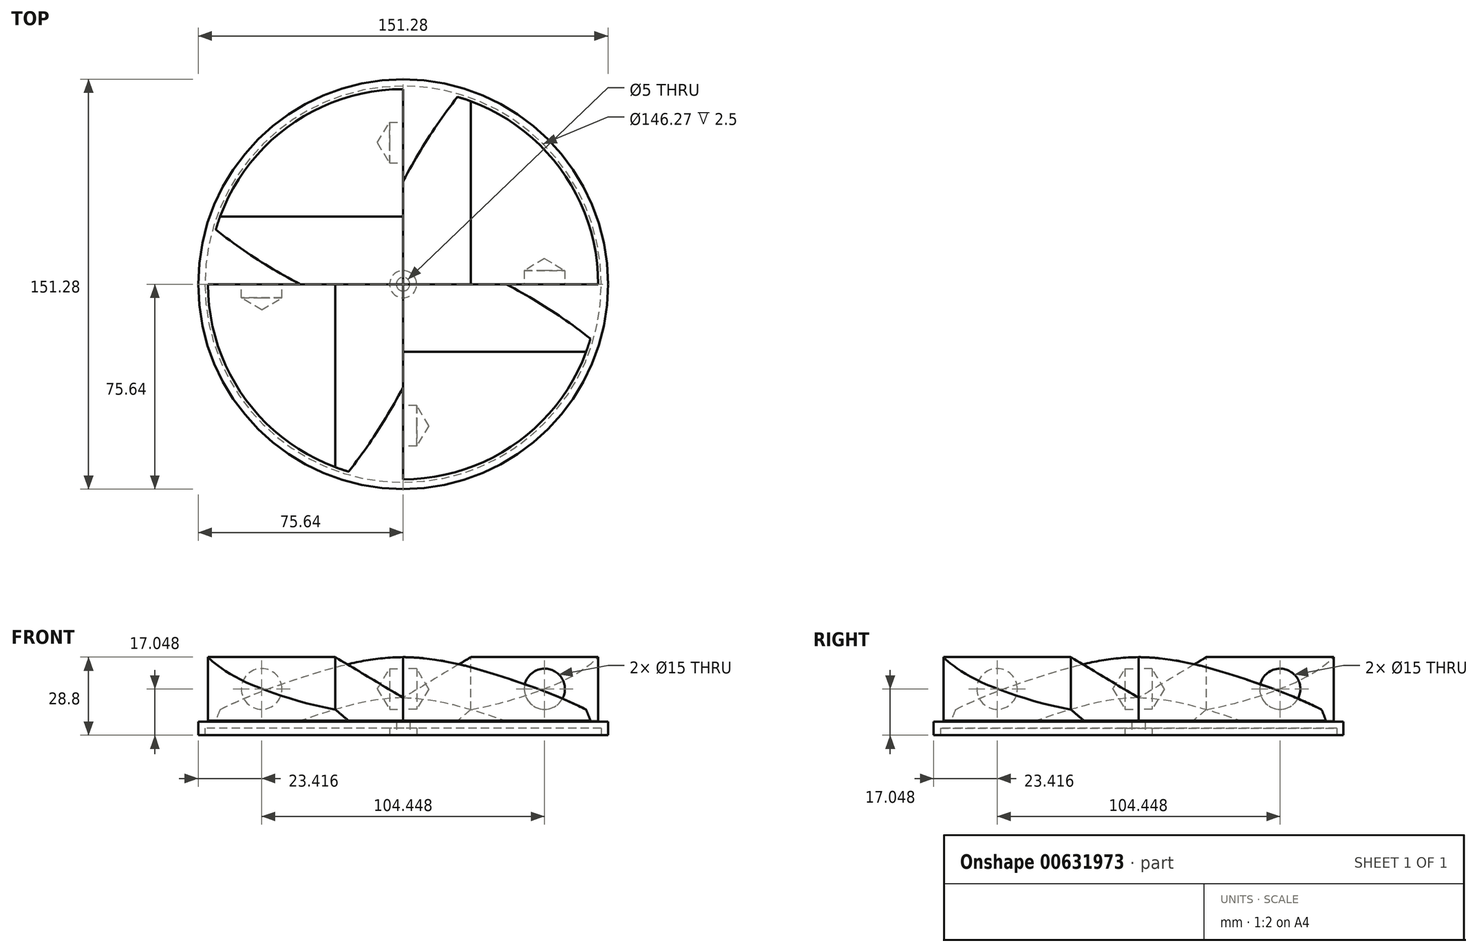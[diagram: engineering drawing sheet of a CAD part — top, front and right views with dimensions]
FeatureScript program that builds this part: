
annotation { "Feature Type Name" : "Feature", "Feature Type Description" : "" }
export const myFeature = defineFeature(function(context is Context, id is Id, definition is map)
    precondition{}
    {
        {
            var Q0;
            Q0=qCreatedBy(makeId("Top.planeOp"),FACE);
            var sketch = newSketch(context, id + "F0", { "sketchPlane" : qUnion([Q0])});
            skCircle(sketch, "E0", {"center": v(0, 0) * mm, "radius": 75.64 * mm});
            skSolve(sketch);
        }
        {
            var Q0;
            Q0=makeQuery(id+"F0.imprint","IMPRINT",FACE,{"disambiguationData":[TD([[makeQuery(id+"F0.imprint","IMPRINT",EDGE,{"derivedFrom":sQuery(id+"F0.wireOp",EDGE,"E0")}),1.0]])]});
            extrude(context, id + "F1", {"entities" : qUnion([Q0]), "depth" : 5 * mm, "offsetDistance" : 25 * mm});
        }
        {
            var Q0;
            Q0=makeQuery(id+"F1.opExtrude","CAP_FACE",FACE,{"disambiguationData":[OSD([sQuery(id+"F0.wireOp",EDGE,"E0")])],"isStart":true});
            var sketch = newSketch(context, id + "F2", { "sketchPlane" : qUnion([Q0])});
            skLineSegment(sketch, "E1", {"start": v(0, 0) * mm, "end": v(-75.64, 0) * mm});
            skSolve(sketch);
        }
        {
            var Q0;
            Q0=sQuery(id+"F2.wireOp",VERTEX,"E1.start");
            var Q1;
            Q1=makeQuery(id+"F1.opExtrude","SWEPT_BODY",BODY,{"disambiguationData":[OSD([sQuery(id+"F0.wireOp",EDGE,"E0")])]});
            hole(context, id + "F3", {"style" : HoleStyle.SIMPLE, "endStyle" : HoleEndStyle.BLIND, "holeDiameter" : 5 * mm, "majorDiameter" : 5 * mm, "holeDepth" : 35 * mm, "isTappedThrough" : true, "tappedDepth" : 12 * mm, "tapClearance" : 3, "locations" : qUnion([Q0]), "scope" : qUnion([Q1])});
        }
        {
            var Q0;
            Q0=qCreatedBy(makeId("Front.planeOp"),FACE);
            var sketch = newSketch(context, id + "F4", { "sketchPlane" : qUnion([Q0])});
            skLineSegment(sketch, "E2", {"start": v(0, 28.8) * mm, "end": v(0, 5.3) * mm});
            skLineSegment(sketch, "E3", {"start": v(0, 5.3) * mm, "end": v(75.31, 5.3) * mm});
            skFitSpline(sketch, "E4", {"points": [v(75.31, 5.3) * mm, v(37.34, 21.33) * mm, v(0, 28.8) * mm], "startDerivative": vector(-82.04, 46.6) * mm, "endDerivative": vector(-85.16, 0.97) * mm});
            skSolve(sketch);
        }
        {
            var Q0;
            Q0=makeQuery(id+"F4.imprint","IMPRINT",FACE,{"disambiguationData":[TD([[makeQuery(id+"F4.imprint","IMPRINT",EDGE,{"derivedFrom":sQuery(id+"F4.wireOp",EDGE,"E2")}),1.0]])]});
            extrude(context, id + "F5", {"entities" : qUnion([Q0]), "depth" : 73 * mm, "offsetDistance" : 25 * mm});
        }
        {
            var Q0;
            Q0=makeQuery(id+"F5.opExtrude","SWEPT_FACE",FACE,{"disambiguationData":[OSD([sQuery(id+"F4.wireOp",EDGE,"E2")])]});
            var sketch = newSketch(context, id + "F6", { "sketchPlane" : qUnion([Q0])});
            skLineSegment(sketch, "E5", {"start": v(20.11, 17.05) * mm, "end": v(52.22, 17.05) * mm});
            skPoint(sketch, "E5.startSnap0", {"position": v(0, 17.05) * mm});
            skSolve(sketch);
        }
        {
            var Q0;
            Q0=sQuery(id+"F6.wireOp",VERTEX,"E5.end");
            var Q1;
            Q1=makeQuery(id+"F5.opExtrude","SWEPT_BODY",BODY,{"disambiguationData":[OSD([sQuery(id+"F4.wireOp",EDGE,"E2"),sQuery(id+"F4.wireOp",EDGE,"E3"),sQuery(id+"F4.wireOp",EDGE,"E4")])]});
            hole(context, id + "F7", {"style" : HoleStyle.SIMPLE, "endStyle" : HoleEndStyle.BLIND, "holeDiameter" : 15 * mm, "majorDiameter" : 5 * mm, "holeDepth" : 5 * mm, "isTappedThrough" : true, "tappedDepth" : 12 * mm, "tapClearance" : 3, "locations" : qUnion([Q0]), "scope" : qUnion([Q1])});
        }
        {
            var Q0;
            Q0=makeQuery(id+"F5.opExtrude","CAP_EDGE",EDGE,{"disambiguationData":[OSD([sQuery(id+"F4.wireOp",EDGE,"E4")])],"isStart":true});
            chamfer(context, id + "F8", {"entities" : qUnion([Q0]), "chamferType" : ChamferType.TWO_OFFSETS, "width1" : 25 * mm, "oppositeDirection" : false, "width2" : 15 * mm, "tangentPropagation" : true});
        }
        {
            var Q0;
            Q0=makeQuery(id+"F5.opExtrude","SWEPT_BODY",BODY,{"disambiguationData":[OSD([sQuery(id+"F4.wireOp",EDGE,"E2"),sQuery(id+"F4.wireOp",EDGE,"E3"),sQuery(id+"F4.wireOp",EDGE,"E4")])]});
            var Q1;
            Q1=makeQuery(id+"F5.opExtrude","CAP_EDGE",EDGE,{"disambiguationData":[OSD([sQuery(id+"F4.wireOp",EDGE,"E2")])],"isStart":true});
            transform(context, id + "F9", {"entities" : qUnion([Q0]), "transformType" : TransformType.ROTATION, "transformAxis" : qUnion([Q1]), "angle" : 90 * degree, "makeCopy" : true});
        }
        {
            var Q0;
            Q0=makeQuery(id+"F9.opPattern","COPY",BODY,{"derivedFrom":makeQuery(id+"F5.opExtrude","SWEPT_BODY",BODY,{"disambiguationData":[OSD([sQuery(id+"F4.wireOp",EDGE,"E2"),sQuery(id+"F4.wireOp",EDGE,"E3"),sQuery(id+"F4.wireOp",EDGE,"E4")])]}),"instanceName":"1"});
            var Q1;
            Q1=makeQuery(id+"F5.opExtrude","CAP_EDGE",EDGE,{"disambiguationData":[OSD([sQuery(id+"F4.wireOp",EDGE,"E2")])],"isStart":true});
            transform(context, id + "F10", {"entities" : qUnion([Q0]), "transformType" : TransformType.ROTATION, "transformAxis" : qUnion([Q1]), "angle" : 90 * degree, "makeCopy" : true});
        }
        {
            var Q0;
            Q0=makeQuery(id+"F10.opPattern","COPY",BODY,{"derivedFrom":makeQuery(id+"F9.opPattern","COPY",BODY,{"derivedFrom":makeQuery(id+"F5.opExtrude","SWEPT_BODY",BODY,{"disambiguationData":[OSD([sQuery(id+"F4.wireOp",EDGE,"E2"),sQuery(id+"F4.wireOp",EDGE,"E3"),sQuery(id+"F4.wireOp",EDGE,"E4")])]}),"instanceName":"1"}),"instanceName":"1"});
            var Q1;
            Q1=makeQuery(id+"F5.opExtrude","CAP_EDGE",EDGE,{"disambiguationData":[OSD([sQuery(id+"F4.wireOp",EDGE,"E2")])],"isStart":true});
            transform(context, id + "F11", {"entities" : qUnion([Q0]), "transformType" : TransformType.ROTATION, "transformAxis" : qUnion([Q1]), "angle" : 90 * degree, "makeCopy" : true});
        }
        {
            var Q0;
            Q0=qCreatedBy(makeId("Top.planeOp"),FACE);
            var sketch = newSketch(context, id + "F12", { "sketchPlane" : qUnion([Q0])});
            skCircle(sketch, "E6", {"center": v(0, 0) * mm, "radius": 72.02 * mm});
            skSolve(sketch);
        }
        {
            var Q0;
            Q0=makeQuery(id+"F12.imprint","IMPRINT",FACE,{"disambiguationData":[TD([[makeQuery(id+"F12.imprint","IMPRINT",EDGE,{"derivedFrom":sQuery(id+"F12.wireOp",EDGE,"E6")}),1.0]])]});
            extrude(context, id + "F13", {"entities" : qUnion([Q0]), "depth" : 44 * mm, "offsetDistance" : 25 * mm});
        }
        {
            var Q0;
            Q0=makeQuery(id+"F13.opExtrude","SWEPT_BODY",BODY,{"disambiguationData":[OSD([sQuery(id+"F12.wireOp",EDGE,"E6")])]});
            var Q1;
            Q1=makeQuery(id+"F10.opPattern","COPY",BODY,{"derivedFrom":makeQuery(id+"F9.opPattern","COPY",BODY,{"derivedFrom":makeQuery(id+"F5.opExtrude","SWEPT_BODY",BODY,{"disambiguationData":[OSD([sQuery(id+"F4.wireOp",EDGE,"E2"),sQuery(id+"F4.wireOp",EDGE,"E3"),sQuery(id+"F4.wireOp",EDGE,"E4")])]}),"instanceName":"1"}),"instanceName":"1"});
            booleanBodies(context, id + "F14", {"operationType" : BooleanOperationType.INTERSECTION, "tools" : qUnion([Q0, Q1])});
        }
        {
            var Q0;
            Q0=makeQuery(id+"F9.opPattern","COPY",BODY,{"derivedFrom":makeQuery(id+"F5.opExtrude","SWEPT_BODY",BODY,{"disambiguationData":[OSD([sQuery(id+"F4.wireOp",EDGE,"E2"),sQuery(id+"F4.wireOp",EDGE,"E3"),sQuery(id+"F4.wireOp",EDGE,"E4")])]}),"instanceName":"1"});
            deleteBodies(context, id + "F15", {"entities" : qUnion([Q0])});
        }
        {
            var Q0;
            Q0=makeQuery(id+"F11.opPattern","COPY",BODY,{"derivedFrom":makeQuery(id+"F10.opPattern","COPY",BODY,{"derivedFrom":makeQuery(id+"F9.opPattern","COPY",BODY,{"derivedFrom":makeQuery(id+"F5.opExtrude","SWEPT_BODY",BODY,{"disambiguationData":[OSD([sQuery(id+"F4.wireOp",EDGE,"E2"),sQuery(id+"F4.wireOp",EDGE,"E3"),sQuery(id+"F4.wireOp",EDGE,"E4")])]}),"instanceName":"1"}),"instanceName":"1"}),"instanceName":"1"});
            deleteBodies(context, id + "F16", {"entities" : qUnion([Q0])});
        }
        {
            var Q0;
            Q0=makeQuery(id+"F5.opExtrude","SWEPT_BODY",BODY,{"disambiguationData":[OSD([sQuery(id+"F4.wireOp",EDGE,"E2"),sQuery(id+"F4.wireOp",EDGE,"E3"),sQuery(id+"F4.wireOp",EDGE,"E4")])]});
            deleteBodies(context, id + "F17", {"entities" : qUnion([Q0])});
        }
        {
            var Q0;
            Q0=makeQuery(id+"F14.opBoolean","INTERSECT",BODY,{"derivedFrom":[makeQuery(id+"F10.opPattern","COPY",BODY,{"derivedFrom":makeQuery(id+"F9.opPattern","COPY",BODY,{"derivedFrom":makeQuery(id+"F5.opExtrude","SWEPT_BODY",BODY,{"disambiguationData":[OSD([sQuery(id+"F4.wireOp",EDGE,"E2"),sQuery(id+"F4.wireOp",EDGE,"E3"),sQuery(id+"F4.wireOp",EDGE,"E4")])]}),"instanceName":"1"}),"instanceName":"1"}),makeQuery(id+"F13.opExtrude","SWEPT_BODY",BODY,{"disambiguationData":[OSD([sQuery(id+"F12.wireOp",EDGE,"E6")])]})]});
            var Q1;
            Q1=makeQuery(id+"F10.opPattern","COPY",EDGE,{"derivedFrom":makeQuery(id+"F9.opPattern","COPY",EDGE,{"derivedFrom":makeQuery(id+"F5.opExtrude","CAP_EDGE",EDGE,{"disambiguationData":[OSD([sQuery(id+"F4.wireOp",EDGE,"E2")])],"isStart":true}),"instanceName":"1"}),"instanceName":"1"});
            transform(context, id + "F18", {"entities" : qUnion([Q0]), "transformType" : TransformType.ROTATION, "transformAxis" : qUnion([Q1]), "angle" : 90 * degree, "makeCopy" : true});
        }
        {
            var Q0;
            Q0=makeQuery(id+"F18.opPattern","COPY",BODY,{"derivedFrom":makeQuery(id+"F14.opBoolean","INTERSECT",BODY,{"derivedFrom":[makeQuery(id+"F10.opPattern","COPY",BODY,{"derivedFrom":makeQuery(id+"F9.opPattern","COPY",BODY,{"derivedFrom":makeQuery(id+"F5.opExtrude","SWEPT_BODY",BODY,{"disambiguationData":[OSD([sQuery(id+"F4.wireOp",EDGE,"E2"),sQuery(id+"F4.wireOp",EDGE,"E3"),sQuery(id+"F4.wireOp",EDGE,"E4")])]}),"instanceName":"1"}),"instanceName":"1"}),makeQuery(id+"F13.opExtrude","SWEPT_BODY",BODY,{"disambiguationData":[OSD([sQuery(id+"F12.wireOp",EDGE,"E6")])]})]}),"instanceName":"1"});
            var Q1;
            Q1=makeQuery(id+"F10.opPattern","COPY",EDGE,{"derivedFrom":makeQuery(id+"F9.opPattern","COPY",EDGE,{"derivedFrom":makeQuery(id+"F5.opExtrude","CAP_EDGE",EDGE,{"disambiguationData":[OSD([sQuery(id+"F4.wireOp",EDGE,"E2")])],"isStart":true}),"instanceName":"1"}),"instanceName":"1"});
            transform(context, id + "F19", {"entities" : qUnion([Q0]), "transformType" : TransformType.ROTATION, "transformAxis" : qUnion([Q1]), "angle" : 90 * degree, "makeCopy" : true});
        }
        {
            var Q0;
            Q0=makeQuery(id+"F19.opPattern","COPY",BODY,{"derivedFrom":makeQuery(id+"F18.opPattern","COPY",BODY,{"derivedFrom":makeQuery(id+"F14.opBoolean","INTERSECT",BODY,{"derivedFrom":[makeQuery(id+"F10.opPattern","COPY",BODY,{"derivedFrom":makeQuery(id+"F9.opPattern","COPY",BODY,{"derivedFrom":makeQuery(id+"F5.opExtrude","SWEPT_BODY",BODY,{"disambiguationData":[OSD([sQuery(id+"F4.wireOp",EDGE,"E2"),sQuery(id+"F4.wireOp",EDGE,"E3"),sQuery(id+"F4.wireOp",EDGE,"E4")])]}),"instanceName":"1"}),"instanceName":"1"}),makeQuery(id+"F13.opExtrude","SWEPT_BODY",BODY,{"disambiguationData":[OSD([sQuery(id+"F12.wireOp",EDGE,"E6")])]})]}),"instanceName":"1"}),"instanceName":"1"});
            var Q1;
            Q1=makeQuery(id+"F10.opPattern","COPY",EDGE,{"derivedFrom":makeQuery(id+"F9.opPattern","COPY",EDGE,{"derivedFrom":makeQuery(id+"F5.opExtrude","CAP_EDGE",EDGE,{"disambiguationData":[OSD([sQuery(id+"F4.wireOp",EDGE,"E2")])],"isStart":true}),"instanceName":"1"}),"instanceName":"1"});
            transform(context, id + "F20", {"entities" : qUnion([Q0]), "transformType" : TransformType.ROTATION, "transformAxis" : qUnion([Q1]), "angle" : 90 * degree, "makeCopy" : true});
        }
        {
            var Q0;
            Q0=makeQuery(id+"F1.opExtrude","CAP_FACE",FACE,{"disambiguationData":[OSD([sQuery(id+"F0.wireOp",EDGE,"E0")])],"isStart":true});
            shell(context, id + "F21", {"entities" : qUnion([Q0]), "thickness" : 2.5 * mm});
        }
    });
